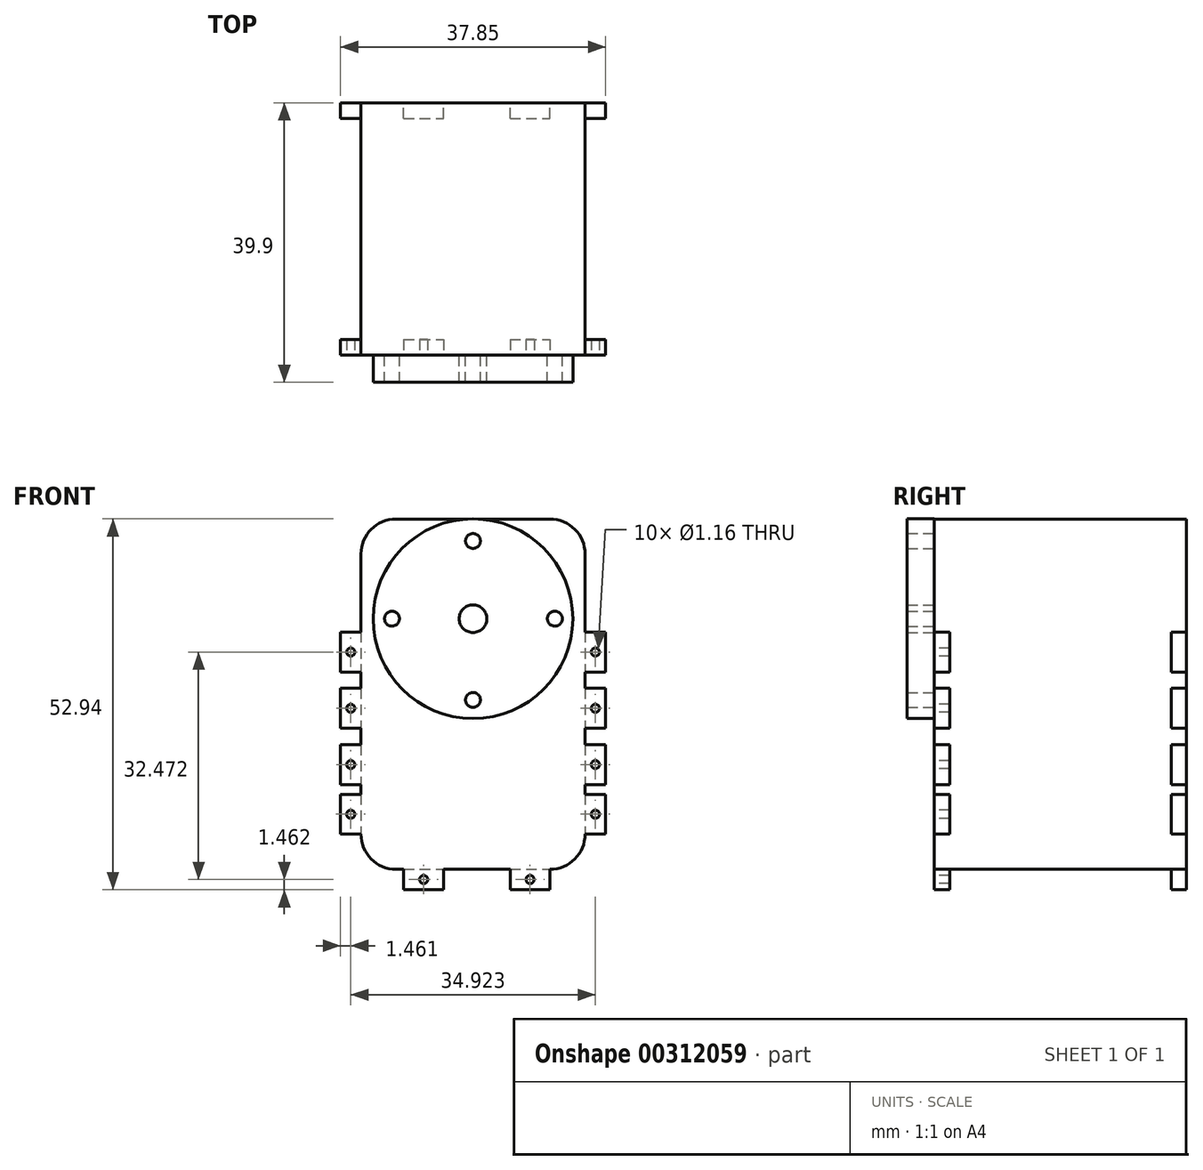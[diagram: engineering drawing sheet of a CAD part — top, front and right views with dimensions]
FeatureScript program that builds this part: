
annotation { "Feature Type Name" : "Feature", "Feature Type Description" : "" }
export const myFeature = defineFeature(function(context is Context, id is Id, definition is map)
    precondition{}
    {
        {
            var Q0;
            Q0=qCreatedBy(makeId("Front.planeOp"),FACE);
            var sketch = newSketch(context, id + "F0", { "sketchPlane" : qUnion([Q0])});
            skLineSegment(sketch, "E0.bottom", {"start": v(2.92, 24.17) * mm, "end": v(34.92, 24.17) * mm});
            skLineSegment(sketch, "E0.top", {"start": v(2.92, -25.83) * mm, "end": v(34.92, -25.83) * mm});
            skLineSegment(sketch, "E0.left", {"start": v(2.92, 24.17) * mm, "end": v(2.92, -25.83) * mm});
            skLineSegment(sketch, "E0.right", {"start": v(34.92, 24.17) * mm, "end": v(34.92, -25.83) * mm});
            skPoint(sketch, "E1.startSnap0", {"position": v(2.92, -0.83) * mm});
            skSolve(sketch);
        }
        {
            var Q0;
            Q0 = qSketchRegion(id + "F0", true);
            extrude(context, id + "F1", {"entities" : qUnion([Q0]), "depth" : 36 * mm});
        }
        {
            var Q0;
            Q0=makeQuery(id+"F1.opExtrude","SWEPT_EDGE",EDGE,{"disambiguationData":[OSD([sQuery(id+"F0.wireOp",EDGE,"E0.bottom"),sQuery(id+"F0.wireOp",EDGE,"E0.left")])]});
            var Q1;
            Q1=makeQuery(id+"F1.opExtrude","SWEPT_EDGE",EDGE,{"disambiguationData":[OSD([sQuery(id+"F0.wireOp",EDGE,"E0.bottom"),sQuery(id+"F0.wireOp",EDGE,"E0.right")])]});
            var Q2;
            Q2=makeQuery(id+"F1.opExtrude","SWEPT_EDGE",EDGE,{"disambiguationData":[OSD([sQuery(id+"F0.wireOp",EDGE,"E0.top"),sQuery(id+"F0.wireOp",EDGE,"E0.right")])]});
            var Q3;
            Q3=makeQuery(id+"F1.opExtrude","SWEPT_EDGE",EDGE,{"disambiguationData":[OSD([sQuery(id+"F0.wireOp",EDGE,"E0.top"),sQuery(id+"F0.wireOp",EDGE,"E0.left")])]});
            fillet(context, id + "F2", {"entities" : qUnion([Q0, Q1, Q2, Q3]), "radius" : 5 * mm, "tangentPropagation" : true, "allowEdgeOverflow" : false});
        }
        {
            var Q0;
            Q0=makeQuery(id+"F1.opExtrude","CAP_FACE",FACE,{"disambiguationData":[OSD([sQuery(id+"F0.wireOp",EDGE,"E0.bottom"),sQuery(id+"F0.wireOp",EDGE,"E0.top"),sQuery(id+"F0.wireOp",EDGE,"E0.left"),sQuery(id+"F0.wireOp",EDGE,"E0.right")])],"isStart":false});
            var sketch = newSketch(context, id + "F3", { "sketchPlane" : qUnion([Q0])});
            skCircle(sketch, "E2", {"center": v(18.92, 9.94) * mm, "radius": 14.25 * mm});
            skCircle(sketch, "E3", {"center": v(18.92, 9.94) * mm, "radius": 1.97 * mm});
            skPoint(sketch, "E4", {"position": v(18.92, 21.04) * mm});
            skPoint(sketch, "E5", {"position": v(7.35, 9.94) * mm});
            skPoint(sketch, "E6", {"position": v(18.92, -1.65) * mm});
            skPoint(sketch, "E7", {"position": v(30.6, 9.94) * mm});
            skCircle(sketch, "E8", {"center": v(7.35, 9.94) * mm, "radius": 1.06 * mm});
            skCircle(sketch, "E9", {"center": v(18.92, 21.04) * mm, "radius": 1.06 * mm});
            skCircle(sketch, "E10", {"center": v(18.92, -1.65) * mm, "radius": 1.06 * mm});
            skCircle(sketch, "E11", {"center": v(30.6, 9.94) * mm, "radius": 1.06 * mm});
            skSolve(sketch);
        }
        {
            var Q0;
            Q0 = qSketchRegion(id + "F3", true);
            extrude(context, id + "F4", {"entities" : qUnion([Q0]), "depth" : 3.9 * mm});
        }
        {
            var Q0;
            Q0=makeQuery(id+"F1.opExtrude","CAP_FACE",FACE,{"disambiguationData":[OSD([sQuery(id+"F0.wireOp",EDGE,"E0.bottom"),sQuery(id+"F0.wireOp",EDGE,"E0.top"),sQuery(id+"F0.wireOp",EDGE,"E0.left"),sQuery(id+"F0.wireOp",EDGE,"E0.right")])],"isStart":false});
            var sketch = newSketch(context, id + "F5", { "sketchPlane" : qUnion([Q0])});
            skLineSegment(sketch, "E12.bottom", {"start": v(2.92, 8.03) * mm, "end": v(0, 8.03) * mm});
            skLineSegment(sketch, "E12.top", {"start": v(2.92, 2.33) * mm, "end": v(0, 2.33) * mm});
            skLineSegment(sketch, "E12.left", {"start": v(2.92, 8.03) * mm, "end": v(2.92, 2.33) * mm});
            skLineSegment(sketch, "E12.right", {"start": v(0, 8.03) * mm, "end": v(0, 2.33) * mm});
            skLineSegment(sketch, "E13.bottom", {"start": v(2.92, 0) * mm, "end": v(0, 0) * mm});
            skLineSegment(sketch, "E13.top", {"start": v(2.92, -5.7) * mm, "end": v(0, -5.7) * mm});
            skLineSegment(sketch, "E13.left", {"start": v(2.92, 0) * mm, "end": v(2.92, -5.7) * mm});
            skLineSegment(sketch, "E13.right", {"start": v(0, 0) * mm, "end": v(0, -5.7) * mm});
            skLineSegment(sketch, "E14.bottom", {"start": v(2.92, -8.03) * mm, "end": v(0, -8.03) * mm});
            skLineSegment(sketch, "E14.top", {"start": v(2.92, -13.73) * mm, "end": v(0, -13.73) * mm});
            skLineSegment(sketch, "E14.left", {"start": v(2.92, -8.03) * mm, "end": v(2.92, -13.73) * mm});
            skLineSegment(sketch, "E14.right", {"start": v(0, -8.03) * mm, "end": v(0, -13.73) * mm});
            skLineSegment(sketch, "E15.bottom", {"start": v(2.92, -15.13) * mm, "end": v(0, -15.13) * mm});
            skLineSegment(sketch, "E15.top", {"start": v(2.92, -20.83) * mm, "end": v(0, -20.83) * mm});
            skLineSegment(sketch, "E15.left", {"start": v(2.92, -15.13) * mm, "end": v(2.92, -20.83) * mm});
            skLineSegment(sketch, "E15.right", {"start": v(0, -15.13) * mm, "end": v(0, -20.83) * mm});
            skPoint(sketch, "E16.oppositeSnap0", {"position": v(1.46, 8.03) * mm});
            skLineSegment(sketch, "E16.bottom", {"start": v(34.92, 2.33) * mm, "end": v(37.85, 2.33) * mm});
            skLineSegment(sketch, "E16.top", {"start": v(34.92, 8.03) * mm, "end": v(37.85, 8.03) * mm});
            skLineSegment(sketch, "E16.left", {"start": v(34.92, 2.33) * mm, "end": v(34.92, 8.03) * mm});
            skLineSegment(sketch, "E16.right", {"start": v(37.85, 2.33) * mm, "end": v(37.85, 8.03) * mm});
            skLineSegment(sketch, "E17.bottom", {"start": v(34.92, -5.7) * mm, "end": v(37.85, -5.7) * mm});
            skLineSegment(sketch, "E17.top", {"start": v(34.92, 0) * mm, "end": v(37.85, 0) * mm});
            skLineSegment(sketch, "E17.left", {"start": v(34.92, -5.7) * mm, "end": v(34.92, 0) * mm});
            skLineSegment(sketch, "E17.right", {"start": v(37.85, -5.7) * mm, "end": v(37.85, 0) * mm});
            skLineSegment(sketch, "E18.bottom", {"start": v(34.92, -13.73) * mm, "end": v(37.85, -13.73) * mm});
            skLineSegment(sketch, "E18.top", {"start": v(34.92, -8.03) * mm, "end": v(37.85, -8.03) * mm});
            skLineSegment(sketch, "E18.left", {"start": v(34.92, -13.73) * mm, "end": v(34.92, -8.03) * mm});
            skLineSegment(sketch, "E18.right", {"start": v(37.85, -13.73) * mm, "end": v(37.85, -8.03) * mm});
            skPoint(sketch, "E19.oppositeSnap0", {"position": v(1.46, -15.13) * mm});
            skPoint(sketch, "E19.oppositeSnap1", {"position": v(37.85, -10.88) * mm});
            skLineSegment(sketch, "E19.bottom", {"start": v(34.92, -20.83) * mm, "end": v(37.85, -20.83) * mm});
            skLineSegment(sketch, "E19.top", {"start": v(34.92, -15.13) * mm, "end": v(37.85, -15.13) * mm});
            skLineSegment(sketch, "E19.left", {"start": v(34.92, -20.83) * mm, "end": v(34.92, -15.13) * mm});
            skLineSegment(sketch, "E19.right", {"start": v(37.85, -20.83) * mm, "end": v(37.85, -15.13) * mm});
            skLineSegment(sketch, "E20.bottom", {"start": v(9.02, -25.83) * mm, "end": v(14.72, -25.83) * mm});
            skLineSegment(sketch, "E20.top", {"start": v(9.02, -28.75) * mm, "end": v(14.72, -28.75) * mm});
            skLineSegment(sketch, "E20.left", {"start": v(9.02, -25.83) * mm, "end": v(9.02, -28.75) * mm});
            skLineSegment(sketch, "E20.right", {"start": v(14.72, -25.83) * mm, "end": v(14.72, -28.75) * mm});
            skLineSegment(sketch, "E21.bottom", {"start": v(29.92, -25.83) * mm, "end": v(24.22, -25.83) * mm});
            skLineSegment(sketch, "E21.top", {"start": v(29.92, -28.75) * mm, "end": v(24.22, -28.75) * mm});
            skLineSegment(sketch, "E21.left", {"start": v(29.92, -25.83) * mm, "end": v(29.92, -28.75) * mm});
            skLineSegment(sketch, "E21.right", {"start": v(24.22, -25.83) * mm, "end": v(24.22, -28.75) * mm});
            skCircle(sketch, "E22", {"center": v(1.47, 5.18) * mm, "radius": 0.58 * mm});
            skPoint(sketch, "E22.centerSnap0", {"position": v(2.92, 5.18) * mm});
            skCircle(sketch, "E23", {"center": v(1.47, -2.85) * mm, "radius": 0.58 * mm});
            skPoint(sketch, "E23.centerSnap0", {"position": v(0, -2.85) * mm});
            skCircle(sketch, "E24", {"center": v(1.47, -10.88) * mm, "radius": 0.58 * mm});
            skPoint(sketch, "E24.centerSnap0", {"position": v(0, -10.88) * mm});
            skCircle(sketch, "E25", {"center": v(1.46, -17.98) * mm, "radius": 0.58 * mm});
            skPoint(sketch, "E25.centerSnap0", {"position": v(0, -17.98) * mm});
            skCircle(sketch, "E26", {"center": v(36.38, 5.18) * mm, "radius": 0.58 * mm});
            skPoint(sketch, "E26.centerSnap0", {"position": v(36.38, 8.03) * mm});
            skPoint(sketch, "E26.centerSnap1", {"position": v(37.85, 5.18) * mm});
            skCircle(sketch, "E27", {"center": v(36.38, -2.85) * mm, "radius": 0.58 * mm});
            skPoint(sketch, "E27.centerSnap0", {"position": v(36.38, 0) * mm});
            skPoint(sketch, "E27.centerSnap1", {"position": v(37.85, -2.85) * mm});
            skCircle(sketch, "E28", {"center": v(36.38, -10.88) * mm, "radius": 0.58 * mm});
            skPoint(sketch, "E28.centerSnap0", {"position": v(36.38, -8.03) * mm});
            skCircle(sketch, "E29", {"center": v(36.38, -17.98) * mm, "radius": 0.58 * mm});
            skPoint(sketch, "E29.centerSnap0", {"position": v(37.85, -17.98) * mm});
            skPoint(sketch, "E29.centerSnap1", {"position": v(36.38, -15.13) * mm});
            skCircle(sketch, "E30", {"center": v(27.07, -27.29) * mm, "radius": 0.58 * mm});
            skPoint(sketch, "E30.centerSnap0", {"position": v(24.22, -27.29) * mm});
            skPoint(sketch, "E30.centerSnap1", {"position": v(27.07, -28.75) * mm});
            skCircle(sketch, "E31", {"center": v(11.87, -27.29) * mm, "radius": 0.58 * mm});
            skPoint(sketch, "E31.centerSnap0", {"position": v(9.02, -27.29) * mm});
            skPoint(sketch, "E31.centerSnap1", {"position": v(11.87, -28.75) * mm});
            skLineSegment(sketch, "E32.MirrorCS", {"start": v(5.85, -8.03) * mm, "end": v(5.85, -13.73) * mm});
            skLineSegment(sketch, "E33.MirrorCS", {"start": v(2.92, -20.83) * mm, "end": v(5.85, -20.83) * mm});
            skPoint(sketch, "E34.MirrorP", {"position": v(4.38, -15.13) * mm});
            skPoint(sketch, "E35.MirrorP", {"position": v(5.85, -10.88) * mm});
            skLineSegment(sketch, "E36.MirrorCS", {"start": v(2.92, -13.73) * mm, "end": v(5.85, -13.73) * mm});
            skCircle(sketch, "E37.MirrorC", {"center": v(4.38, -17.98) * mm, "radius": 0.58 * mm});
            skLineSegment(sketch, "E38.MirrorCS", {"start": v(2.92, -15.13) * mm, "end": v(5.85, -15.13) * mm});
            skPoint(sketch, "E39.MirrorP", {"position": v(5.85, -2.85) * mm});
            skPoint(sketch, "E40.MirrorP", {"position": v(5.85, -17.98) * mm});
            skLineSegment(sketch, "E41.MirrorCS", {"start": v(5.85, 8.03) * mm, "end": v(5.85, 2.33) * mm});
            skLineSegment(sketch, "E42.MirrorCS", {"start": v(5.85, -15.13) * mm, "end": v(5.85, -20.83) * mm});
            skLineSegment(sketch, "E43.MirrorCS", {"start": v(5.85, 0) * mm, "end": v(5.85, -5.7) * mm});
            skPoint(sketch, "E44.MirrorP", {"position": v(4.38, 8.03) * mm});
            skSolve(sketch);
        }
        {
            var Q0;
            Q0 = qSketchRegion(id + "F5", true);
            extrude(context, id + "F6", {"entities" : qUnion([Q0]), "operationType" : NewBodyOperationType.ADD, "oppositeDirection" : true, "depth" : 2.2 * mm});
        }
        {
            var Q0;
            Q0=makeQuery(id+"F0.imprint","IMPRINT",FACE,{"disambiguationData":[TD([[makeQuery(id+"F0.imprint","IMPRINT",EDGE,{"derivedFrom":sQuery(id+"F0.wireOp",EDGE,"E0.bottom")}),-1.0]])]});
            var sketch = newSketch(context, id + "F7", { "sketchPlane" : qUnion([Q0])});
            skLineSegment(sketch, "E45.bottom", {"start": v(34.92, 8.03) * mm, "end": v(37.85, 8.03) * mm});
            skLineSegment(sketch, "E45.top", {"start": v(34.92, 2.33) * mm, "end": v(37.85, 2.33) * mm});
            skLineSegment(sketch, "E45.left", {"start": v(34.92, 8.03) * mm, "end": v(34.92, 2.33) * mm});
            skLineSegment(sketch, "E45.right", {"start": v(37.85, 8.03) * mm, "end": v(37.85, 2.33) * mm});
            skLineSegment(sketch, "E46.bottom", {"start": v(34.92, -5.7) * mm, "end": v(37.85, -5.7) * mm});
            skLineSegment(sketch, "E46.top", {"start": v(34.92, 0) * mm, "end": v(37.85, 0) * mm});
            skLineSegment(sketch, "E46.left", {"start": v(34.92, -5.7) * mm, "end": v(34.92, 0) * mm});
            skLineSegment(sketch, "E46.right", {"start": v(37.85, -5.7) * mm, "end": v(37.85, 0) * mm});
            skLineSegment(sketch, "E47.bottom", {"start": v(34.92, -13.73) * mm, "end": v(37.85, -13.73) * mm});
            skLineSegment(sketch, "E47.top", {"start": v(34.92, -8.03) * mm, "end": v(37.85, -8.03) * mm});
            skLineSegment(sketch, "E47.left", {"start": v(34.92, -13.73) * mm, "end": v(34.92, -8.03) * mm});
            skLineSegment(sketch, "E47.right", {"start": v(37.85, -13.73) * mm, "end": v(37.85, -8.03) * mm});
            skLineSegment(sketch, "E48.bottom", {"start": v(34.92, -20.83) * mm, "end": v(37.85, -20.83) * mm});
            skLineSegment(sketch, "E48.top", {"start": v(34.92, -15.13) * mm, "end": v(37.85, -15.13) * mm});
            skLineSegment(sketch, "E48.left", {"start": v(34.92, -20.83) * mm, "end": v(34.92, -15.13) * mm});
            skLineSegment(sketch, "E48.right", {"start": v(37.85, -20.83) * mm, "end": v(37.85, -15.13) * mm});
            skLineSegment(sketch, "E49.bottom", {"start": v(2.92, 2.33) * mm, "end": v(0, 2.33) * mm});
            skLineSegment(sketch, "E49.top", {"start": v(2.92, 8.03) * mm, "end": v(0, 8.03) * mm});
            skLineSegment(sketch, "E49.left", {"start": v(2.92, 2.33) * mm, "end": v(2.92, 8.03) * mm});
            skLineSegment(sketch, "E49.right", {"start": v(0, 2.33) * mm, "end": v(0, 8.03) * mm});
            skLineSegment(sketch, "E50.bottom", {"start": v(2.92, -5.7) * mm, "end": v(0, -5.7) * mm});
            skLineSegment(sketch, "E50.top", {"start": v(2.92, 0) * mm, "end": v(0, 0) * mm});
            skLineSegment(sketch, "E50.left", {"start": v(2.92, -5.7) * mm, "end": v(2.92, 0) * mm});
            skLineSegment(sketch, "E50.right", {"start": v(0, -5.7) * mm, "end": v(0, 0) * mm});
            skLineSegment(sketch, "E51.bottom", {"start": v(2.92, -13.73) * mm, "end": v(0, -13.73) * mm});
            skLineSegment(sketch, "E51.top", {"start": v(2.92, -8.03) * mm, "end": v(0, -8.03) * mm});
            skLineSegment(sketch, "E51.left", {"start": v(2.92, -13.73) * mm, "end": v(2.92, -8.03) * mm});
            skLineSegment(sketch, "E51.right", {"start": v(0, -13.73) * mm, "end": v(0, -8.03) * mm});
            skLineSegment(sketch, "E52.bottom", {"start": v(2.92, -20.83) * mm, "end": v(0, -20.83) * mm});
            skLineSegment(sketch, "E52.top", {"start": v(2.92, -15.13) * mm, "end": v(0, -15.13) * mm});
            skLineSegment(sketch, "E52.left", {"start": v(2.92, -20.83) * mm, "end": v(2.92, -15.13) * mm});
            skLineSegment(sketch, "E52.right", {"start": v(0, -20.83) * mm, "end": v(0, -15.13) * mm});
            skLineSegment(sketch, "E53.bottom", {"start": v(24.22, -25.83) * mm, "end": v(29.92, -25.83) * mm});
            skLineSegment(sketch, "E53.top", {"start": v(24.22, -28.75) * mm, "end": v(29.92, -28.75) * mm});
            skLineSegment(sketch, "E53.left", {"start": v(24.22, -25.83) * mm, "end": v(24.22, -28.75) * mm});
            skLineSegment(sketch, "E53.right", {"start": v(29.92, -25.83) * mm, "end": v(29.92, -28.75) * mm});
            skLineSegment(sketch, "E54.bottom", {"start": v(9.02, -25.83) * mm, "end": v(14.72, -25.83) * mm});
            skLineSegment(sketch, "E54.top", {"start": v(9.02, -28.75) * mm, "end": v(14.72, -28.75) * mm});
            skLineSegment(sketch, "E54.left", {"start": v(9.02, -25.83) * mm, "end": v(9.02, -28.75) * mm});
            skLineSegment(sketch, "E54.right", {"start": v(14.72, -25.83) * mm, "end": v(14.72, -28.75) * mm});
            skLineSegment(sketch, "E55", {"start": v(36.38, 8.03) * mm, "end": v(36.38, -20.83) * mm, "construction": true});
            skLineSegment(sketch, "E56", {"start": v(1.46, 8.03) * mm, "end": v(1.46, -20.83) * mm, "construction": true});
            skPoint(sketch, "E57", {"position": v(36.38, 8.03) * mm});
            skPoint(sketch, "E58", {"position": v(36.38, 2.33) * mm});
            skPoint(sketch, "E59", {"position": v(36.38, 0) * mm});
            skPoint(sketch, "E60", {"position": v(36.38, -5.7) * mm});
            skPoint(sketch, "E61", {"position": v(36.38, -8.03) * mm});
            skPoint(sketch, "E62", {"position": v(36.38, -13.73) * mm});
            skPoint(sketch, "E63", {"position": v(36.38, -15.13) * mm});
            skPoint(sketch, "E64", {"position": v(36.38, -20.83) * mm});
            skSolve(sketch);
        }
        {
            var Q0;
            Q0 = qSketchRegion(id + "F7", true);
            extrude(context, id + "F8", {"entities" : qUnion([Q0]), "operationType" : NewBodyOperationType.ADD, "depth" : 2.2 * mm});
        }
    });
